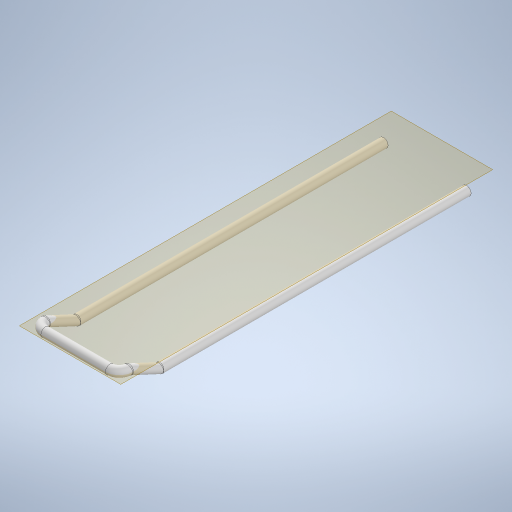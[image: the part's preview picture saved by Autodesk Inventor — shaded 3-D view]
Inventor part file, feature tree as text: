
AUTODESK INVENTOR PART (.ipt)
format: ipt  version: 2024.1 (Build 281209000, 209)  size: 344,064 bytes
history: native  units: mm
features: sketch x5, projected_geometry x5, sweep x2, fillet x2, extrude x1, plane x1, other x1
ambient origin geometry x8: Origin, YZ Plane, XZ Plane, XY Plane, X Axis, Y Axis, Z Axis, Center Point
bodies: Solid1 (feature_tree)
feature tree (17):
  extrude  "Extrusion1"  Depth=135.0mm
  sweep  "Sweep1"
  fillet  "Fillet1"  Radius=50.0mm
  plane  "Work Plane1"
  sweep  "Sweep2"
  fillet  "Fillet2"  Radius=6.0mm
  sketch  "Sketch2"  dims[d0=15.0mm d1=135.0mm]
  sketch  "Sketch3"  dims[d2=67.5mm d3=500.0mm d4=0.0mm d5=50.0mm]
  sketch  "Sketch4"  dims[d6=4.363323mm d7=0.0mm d8=0.0mm d9=6.0mm]
  projected_geometry  "Projected Loop1"
  projected_geometry  "Projected Loop2"
  other  "Work Point1"
  sketch  "Sketch5"  dims[d10=15.0mm]
  projected_geometry  "Projected Loop3"
  sketch  "Sketch6"  dims[d11=15.0mm d12=0.0mm d13=0.0mm d14=6.0mm]
  projected_geometry  "Projected Loop4"
  projected_geometry  "Projected Loop5"
